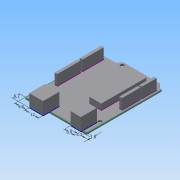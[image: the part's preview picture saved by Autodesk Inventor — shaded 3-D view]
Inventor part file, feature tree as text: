
AUTODESK INVENTOR PART (.ipt)
format: ipt  version: 2015 (Build 190159000, 159)  size: 149,504 bytes
history: native  units: in
note: dims shown in document units (in); Inventor stores cm internally (conversion verified against a paired STEP export)
features: extrude x4, sketch x2
ambient origin geometry x8: Origin, YZ Plane, XZ Plane, XY Plane, X Axis, Y Axis, Z Axis, Center Point
bodies: Solid1 (feature_tree)
feature tree (6):
  extrude  "board"  Depth=2.0984in
  sketch  "Sketch2"  dims[d6=0.0433in d8=1.0984in d9=0.5984in d10=2.7008in d11=0.126in d12=2.0in d13=0.185in d15=0.0984in d17=0.5512in d18=1.4567in d19=1.5748in d20=0.0787in d21=0.1969in d22=2.5591in d23=0.063in d24=0.0in d25=0.378in d26=0.4724in d27=0.1299in d28=0.3504in d29=0.0709in d30=0.2441in d31=0.4291in d32=0.0in d33=0.1969in d34=0.0in d35=0.3543in d36=0.0in]
  extrude  "Extrusion2"  Depth=0.3543in
  extrude  "Extrusion3"  Depth=0.3543in
  extrude  "Extrusion4"  Depth=2.7008in
  sketch  "Sketch1"  dims[d2=2.0984in d5=2.0433in]
